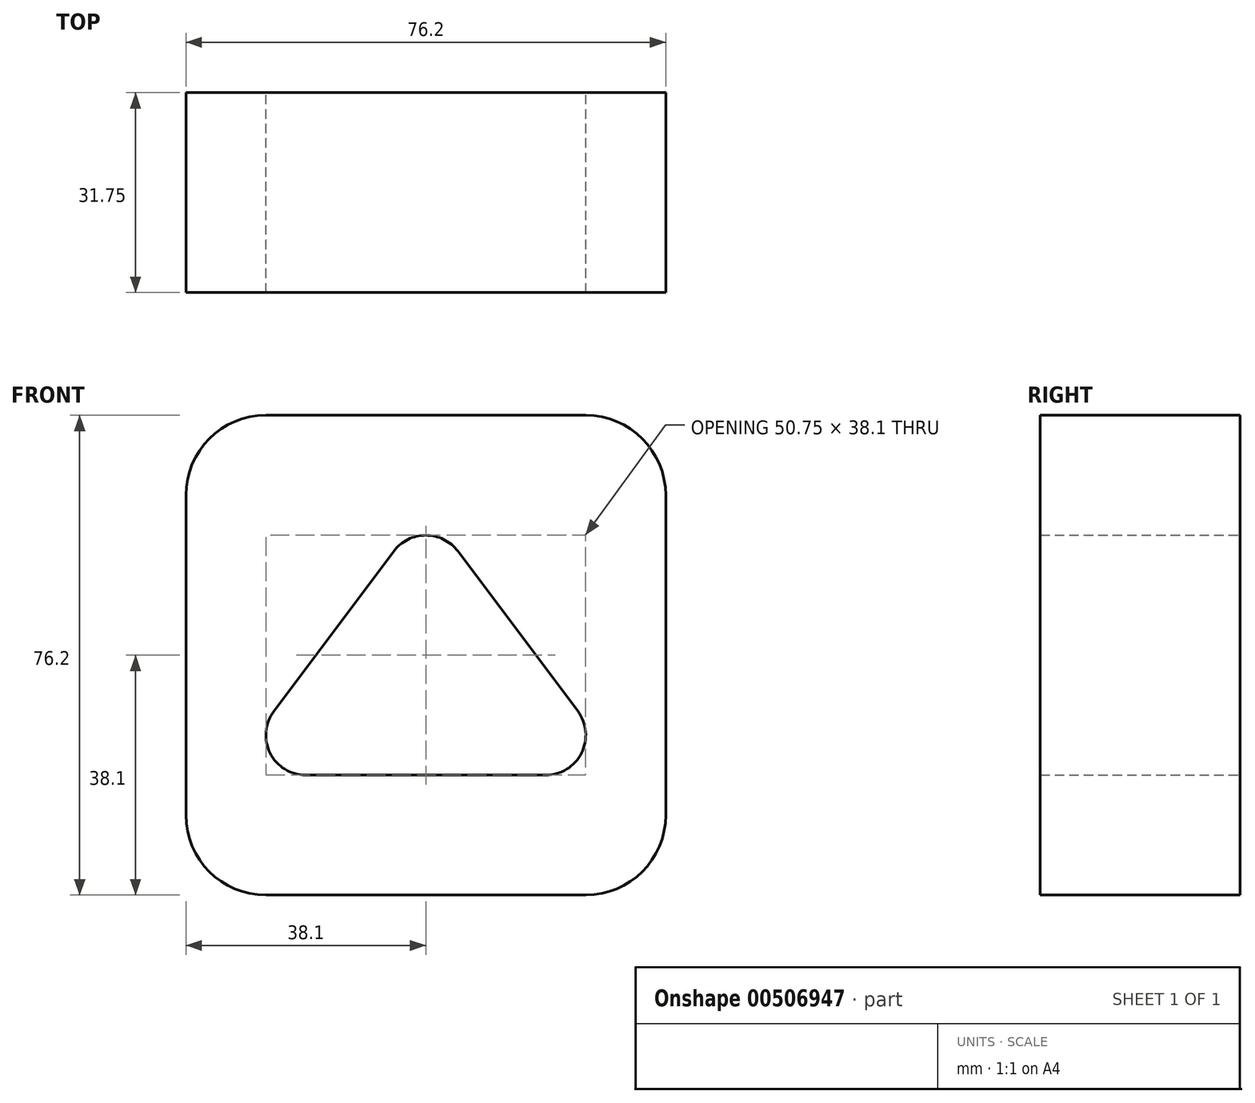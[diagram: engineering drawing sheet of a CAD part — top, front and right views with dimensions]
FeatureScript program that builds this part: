
annotation { "Feature Type Name" : "Feature", "Feature Type Description" : "" }
export const myFeature = defineFeature(function(context is Context, id is Id, definition is map)
    precondition{}
    {
        {
            var Q0;
            Q0=qCreatedBy(makeId("Front.planeOp"),FACE);
            var sketch = newSketch(context, id + "F0", { "sketchPlane" : qUnion([Q0])});
            skLineSegment(sketch, "E0", {"start": v(12.7, 0) * mm, "end": v(63.5, 0) * mm});
            skLineSegment(sketch, "E1", {"start": v(76.2, 12.7) * mm, "end": v(76.2, 63.5) * mm});
            skLineSegment(sketch, "E2", {"start": v(63.5, 76.2) * mm, "end": v(12.7, 76.2) * mm});
            skLineSegment(sketch, "E3", {"start": v(0, 76.2) * mm, "end": v(0, 12.7) * mm});
            skArc(sketch, "E4", {"start": v(13.97, 29.21) * mm, "mid": v(13.37, 22.56) * mm, "end": v(19.05, 19.05) * mm});
            skArc(sketch, "E5", {"start": v(57.15, 19.05) * mm, "mid": v(62.83, 22.56) * mm, "end": v(62.23, 29.21) * mm});
            skArc(sketch, "E6", {"start": v(43.18, 54.6) * mm, "mid": v(38.1, 57.15) * mm, "end": v(33.02, 54.6) * mm});
            skLineSegment(sketch, "E7", {"start": v(33.02, 54.6) * mm, "end": v(13.97, 29.21) * mm});
            skLineSegment(sketch, "E8", {"start": v(43.18, 54.6) * mm, "end": v(62.23, 29.21) * mm});
            skLineSegment(sketch, "E9", {"start": v(19.05, 19.05) * mm, "end": v(57.15, 19.05) * mm});
            skArc(sketch, "E10", {"start": v(12.7, 76.2) * mm, "mid": v(3.72, 72.48) * mm, "end": v(0, 63.5) * mm});
            skArc(sketch, "E11", {"start": v(76.2, 63.5) * mm, "mid": v(72.48, 72.48) * mm, "end": v(63.5, 76.2) * mm});
            skPoint(sketch, "E12.visualSharp", {"position": v(0, 0) * mm});
            skArc(sketch, "E12.filletArc", {"start": v(0, 12.7) * mm, "mid": v(3.72, 3.72) * mm, "end": v(12.7, 0) * mm});
            skPoint(sketch, "E13.visualSharp", {"position": v(76.2, 0) * mm});
            skArc(sketch, "E13.filletArc", {"start": v(63.5, 0) * mm, "mid": v(72.48, 3.72) * mm, "end": v(76.2, 12.7) * mm});
            skSolve(sketch);
        }
        {
            var Q0;
            Q0=makeQuery(id+"F0.imprint","IMPRINT",FACE,{"disambiguationData":[TD([[makeQuery(id+"F0.imprint","IMPRINT",EDGE,{"derivedFrom":sQuery(id+"F0.wireOp",EDGE,"E0")}),1.0]])]});
            extrude(context, id + "F1", {"entities" : qUnion([Q0]), "depth" : 31.75 * mm, "offsetDistance" : 25.4 * mm});
        }
    });
